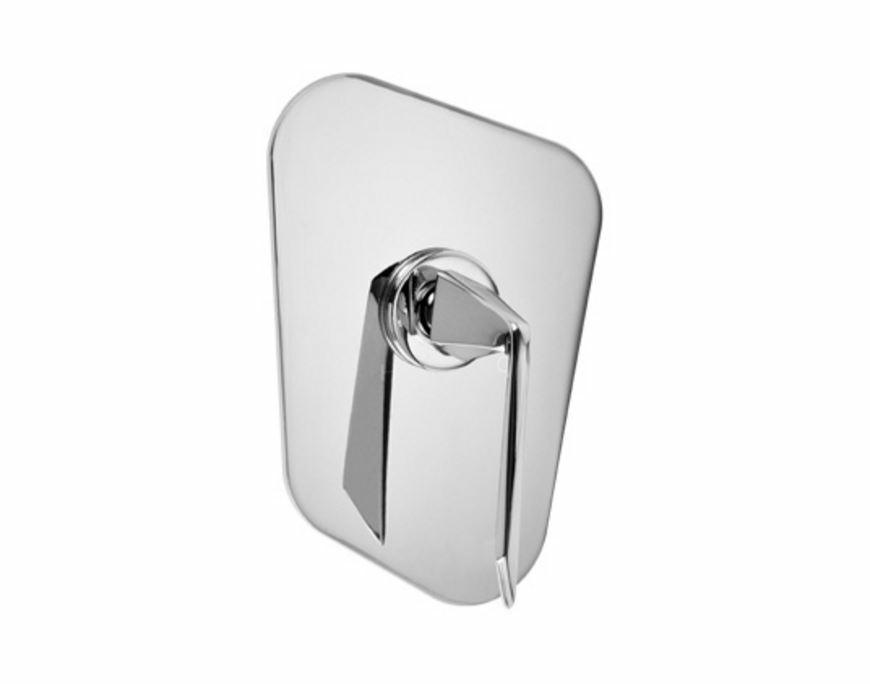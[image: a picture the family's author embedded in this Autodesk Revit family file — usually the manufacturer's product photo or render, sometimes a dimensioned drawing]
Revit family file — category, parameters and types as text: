
# Revit family: Monomando de Regadera PIU-200
name_source: partatom
category: Aparatos sanitarios
revit_build: Autodesk Revit 2016 (Build: 20150220_1215(x64)
units: mm (PartAtom-declared; Revit-internal decimal feet)

## family parameters
Compartido = Sí
Corte con vacíos al cargar = No
Cota de conector redondo = Diámetro de uso
Número OmniClass = 23.45.05.14.99
Punto de cálculo de habitación = Sí
Se basa en plano de trabajo = Sí
Siempre vertical = Sí
Tipo de pieza = Normal
Título OmniClass = Other Sanitary Washing Plumbing Fixtures

## types (1)
- PIU-200
    Brass Chromed = Brass
    Cartucho = Cartucho monomando cerámico  Ø40mm
    Comentarios de tipo = Monomando Piura
    Descripción = Monomando para Regadera sin Balanceo de Presión sin Desviador
    Elevación por defecto = 1"
    Fabricante = HELVEX S.A. DE C.V.
    Garantía = El producto HELVEX está garantizado como libre de defectos en materiales y procesos de fabricación. El producto HELVEX está garantizado, en lo que se refiere a los acabados; por un periodo de 10 años en los acabados cromo y duravex, y por 2 años en cabados diferentes al cromo, a partir de la fecha de compra indicada en la factura.
    Imagen de tipo = PIU-200.JPG
    Instalación = ½" - 14 NPT
    Modelo = PIU-200
    Operación = Para abrir el flujo de agua levante la palanca maneral y gire para regular la temperatura.
    Presión máxima de trabajo = 85.3 psi
    Presión mínima de trabajo = 14.2 psi
    Support Base Diameter = 5"
    Total Height = 8"
    URL = http://www.helvex.com.mx

## geometry (parser evidence)
native form markers: Sweep x3
no freeform markers — native parametric forms only
